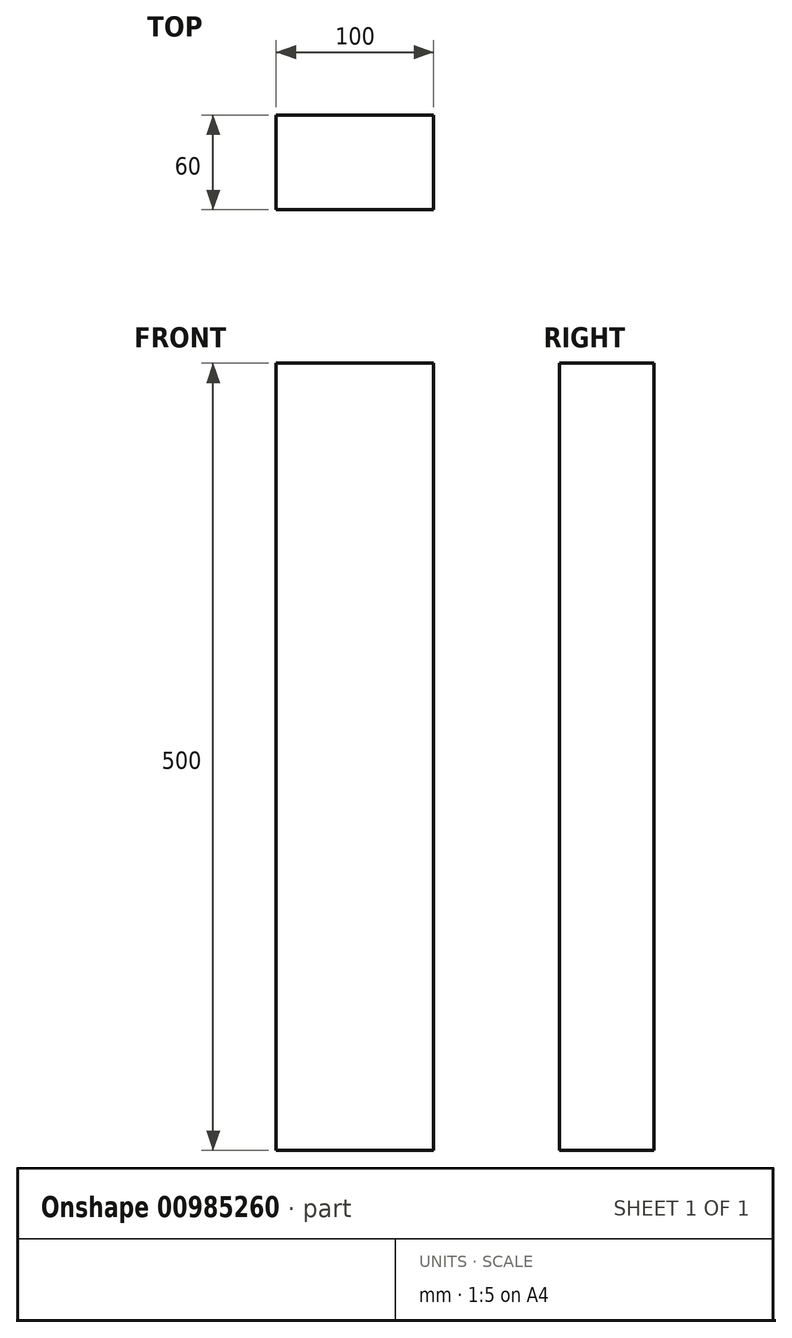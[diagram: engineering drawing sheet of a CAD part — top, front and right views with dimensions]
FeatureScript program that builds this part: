
annotation { "Feature Type Name" : "Feature", "Feature Type Description" : "" }
export const myFeature = defineFeature(function(context is Context, id is Id, definition is map)
    precondition{}
    {
        {
            var Q0;
            Q0=qCreatedBy(makeId("Top.planeOp"),FACE);
            var sketch = newSketch(context, id + "F0", { "sketchPlane" : qUnion([Q0])});
            skLineSegment(sketch, "E0.bottom", {"start": v(0, 0) * mm, "end": v(100, 0) * mm});
            skLineSegment(sketch, "E0.top", {"start": v(0, 60) * mm, "end": v(100, 60) * mm});
            skLineSegment(sketch, "E0.left", {"start": v(0, 0) * mm, "end": v(0, 60) * mm});
            skLineSegment(sketch, "E0.right", {"start": v(100, 0) * mm, "end": v(100, 60) * mm});
            skSolve(sketch);
        }
        {
            var Q0;
            Q0 = qSketchRegion(id + "F0", true);
            extrude(context, id + "F1", {"entities" : qUnion([Q0]), "depth" : 500 * mm, "offsetDistance" : 25 * mm});
        }
    });
